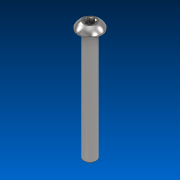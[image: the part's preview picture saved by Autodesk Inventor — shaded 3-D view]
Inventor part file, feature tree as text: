
AUTODESK INVENTOR PART (.ipt)
format: ipt  version: 2022.2 (Build 262287000, 287)  size: 170,496 bytes
history: native  units: in
note: dims shown in document units (in); Inventor stores cm internally (conversion verified against a paired STEP export)
features: direct_edit x1, chamfer x1, move_body x1
ambient origin geometry x8: Origin, YZ Plane, XZ Plane, XY Plane, X Axis, Y Axis, Z Axis, Center Point
bodies: Solid1 (feature_tree)
feature tree (3):
  direct_edit  "Direct Edit1"
  chamfer  "Chamfer2"  [1 undecoded]
  move_body  "Move1"
note: 1 required parameter value undecoded (feature->parameter linkage not recoverable at this tier; creation-order binding heuristic only, values carry confidence <= 0.55)
